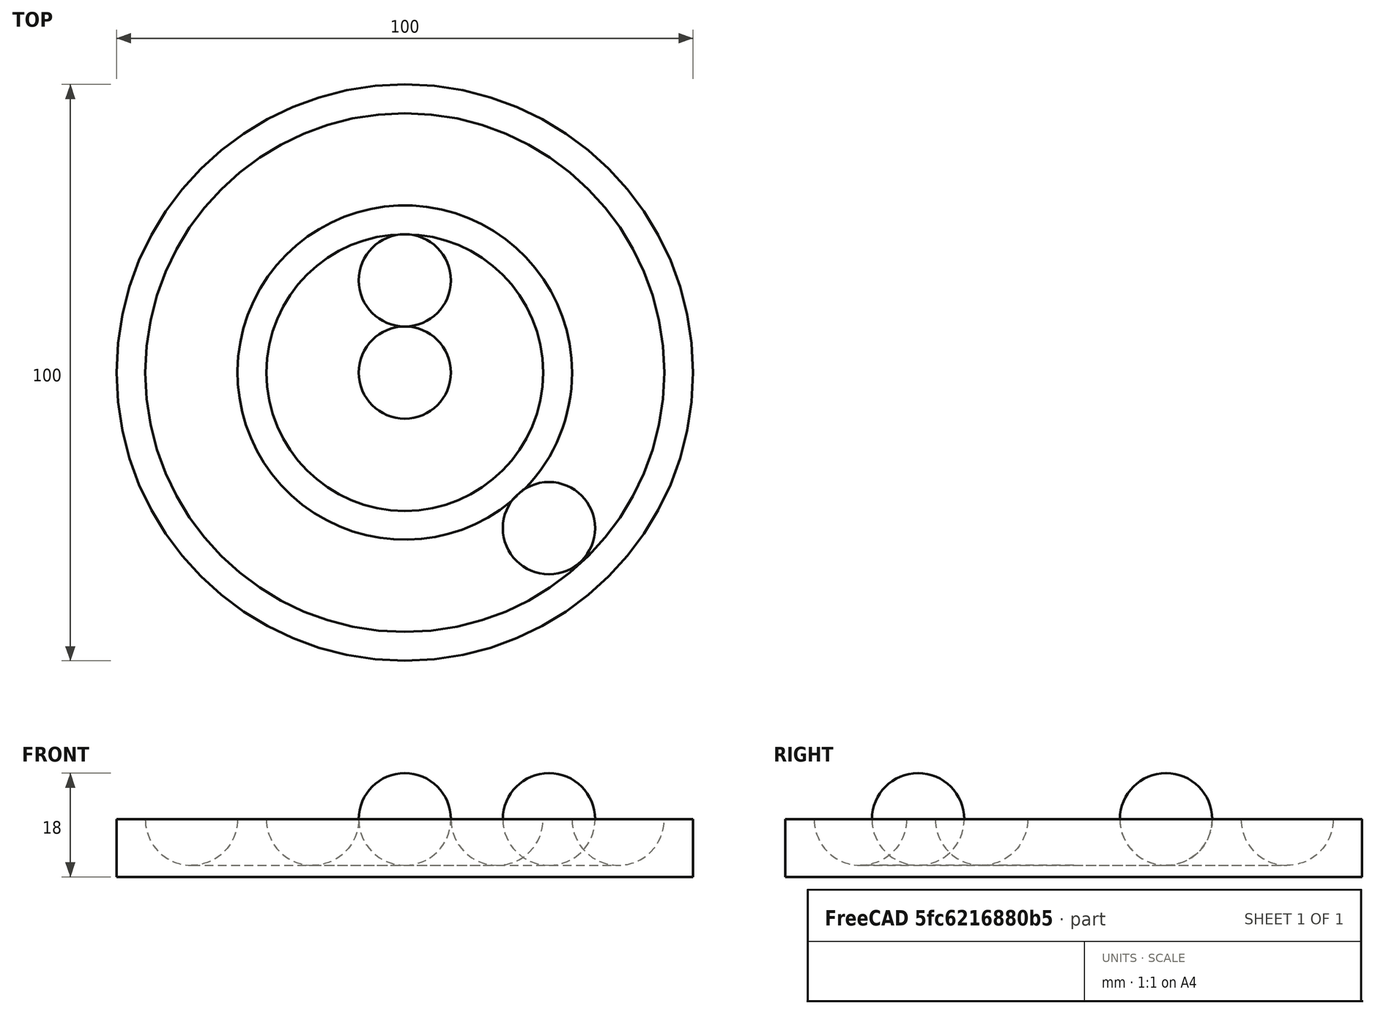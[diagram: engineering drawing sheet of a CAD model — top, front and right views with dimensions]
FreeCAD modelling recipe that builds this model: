
FCSTD DOCUMENT  (FreeCAD 1.0R39319 (Git))
Label: ojt1_t15r02_toolholders
License: All rights reserved
LicenseURL: https://en.wikipedia.org/wiki/All_rights_reserved
objects: Part::Torus×2, Part::Cut×2, Part::Sphere×2, Part::Cylinder×1
note: 7 computed .brp shape members not serialized (recipe doc carries the construction recipe); baked Part::Feature solids carry a one-line shape summary decoded from their .brp

FEATURE [Part::Cylinder] Cylinder  label="Cilindre"
  Angle = 360
  AttacherType = Attacher::AttachEngine3D
  FirstAngle = 0
  Height = 10
  Radius = 50
  SecondAngle = 0
FEATURE [Part::Torus] Torus
  Angle1 = -180
  Angle2 = 180
  Angle3 = 360
  AttacherType = Attacher::AttachEngine3D
  Placement = pos=(0,0,10) rot=(0,0,1;0rad)
  Radius1 = 16
  Radius2 = 8
FEATURE [Part::Cut] Cut
  Base = -> Cylinder
  Tool = -> Torus
FEATURE [Part::Torus] Torus001
  Angle1 = -180
  Angle2 = 180
  Angle3 = 360
  AttacherType = Attacher::AttachEngine3D
  Placement = pos=(0,0,10) rot=(0,0,1;0rad)
  Radius1 = 37
  Radius2 = 8
FEATURE [Part::Cut] Cut001
  Base = -> Cut
  Tool = -> Torus001
FEATURE [Part::Sphere] Sphere  label="Esfera"
  Angle1 = -90
  Angle2 = 90
  Angle3 = 360
  AttacherType = Attacher::AttachEngine3D
  Placement = pos=(0,16,10) rot=(0,0,1;0rad)
  Radius = 8
FEATURE [Part::Sphere] Sphere001  label="Esfera001"
  Angle1 = -90
  Angle2 = 90
  Angle3 = 360
  AttacherType = Attacher::AttachEngine3D
  Placement = pos=(25,-27,10) rot=(0,0,1;0rad)
  Radius = 8
